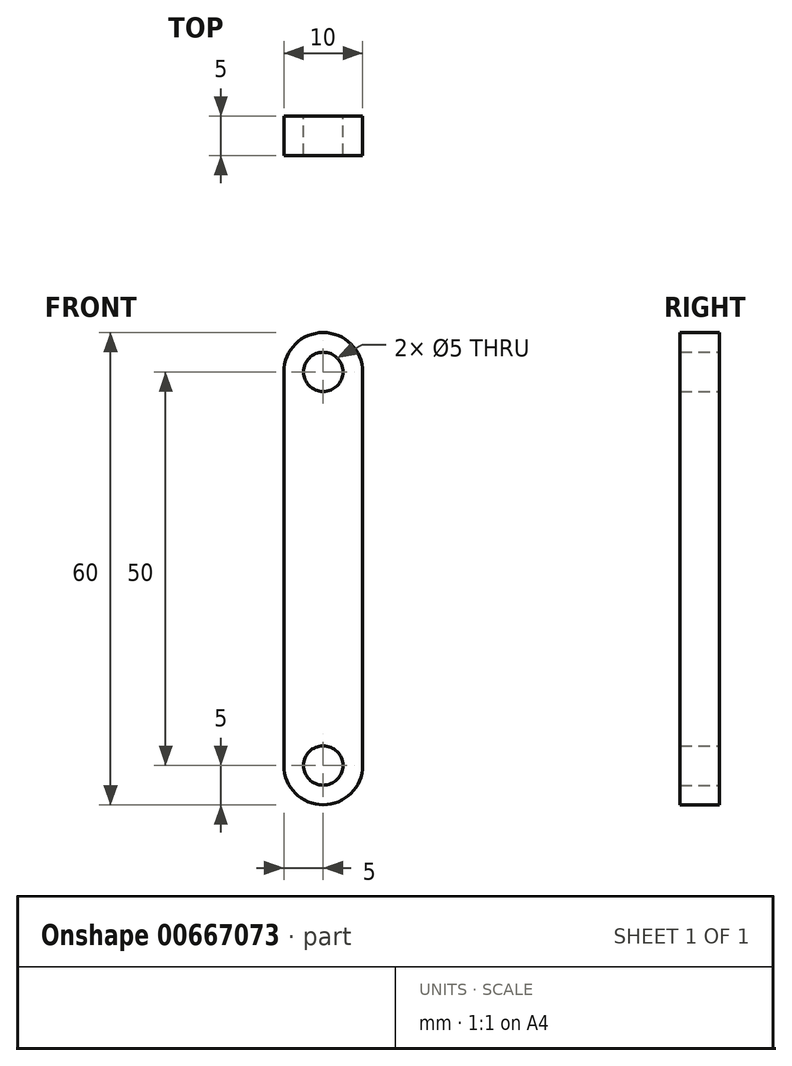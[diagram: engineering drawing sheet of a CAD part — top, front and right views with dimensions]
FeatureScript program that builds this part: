
annotation { "Feature Type Name" : "Feature", "Feature Type Description" : "" }
export const myFeature = defineFeature(function(context is Context, id is Id, definition is map)
    precondition{}
    {
        {
            var Q0;
            Q0=qCreatedBy(makeId("Front.planeOp"),FACE);
            var sketch = newSketch(context, id + "F0", { "sketchPlane" : qUnion([Q0])});
            skArc(sketch, "E0", {"start": v(-5, 0) * mm, "mid": v(0, -5) * mm, "end": v(5, 0) * mm});
            skCircle(sketch, "E1", {"center": v(0, 0) * mm, "radius": 2.5 * mm});
            skArc(sketch, "E2", {"start": v(5, 50) * mm, "mid": v(0, 55) * mm, "end": v(-5, 50) * mm});
            skCircle(sketch, "E3", {"center": v(0, 50) * mm, "radius": 2.5 * mm});
            skLineSegment(sketch, "E4", {"start": v(-5, 50) * mm, "end": v(-5, 0) * mm});
            skLineSegment(sketch, "E5", {"start": v(5, 50) * mm, "end": v(5, 0) * mm});
            skSolve(sketch);
        }
        {
            var Q0;
            Q0=makeQuery(id+"F0.imprint","IMPRINT",FACE,{"disambiguationData":[TD([[makeQuery(id+"F0.imprint","IMPRINT",EDGE,{"derivedFrom":sQuery(id+"F0.wireOp",EDGE,"E0")}),1.0]])]});
            extrude(context, id + "F1", {"entities" : qUnion([Q0]), "endBound" : BoundingType.SYMMETRIC, "depth" : 5 * mm, "offsetDistance" : 25 * mm});
        }
    });
